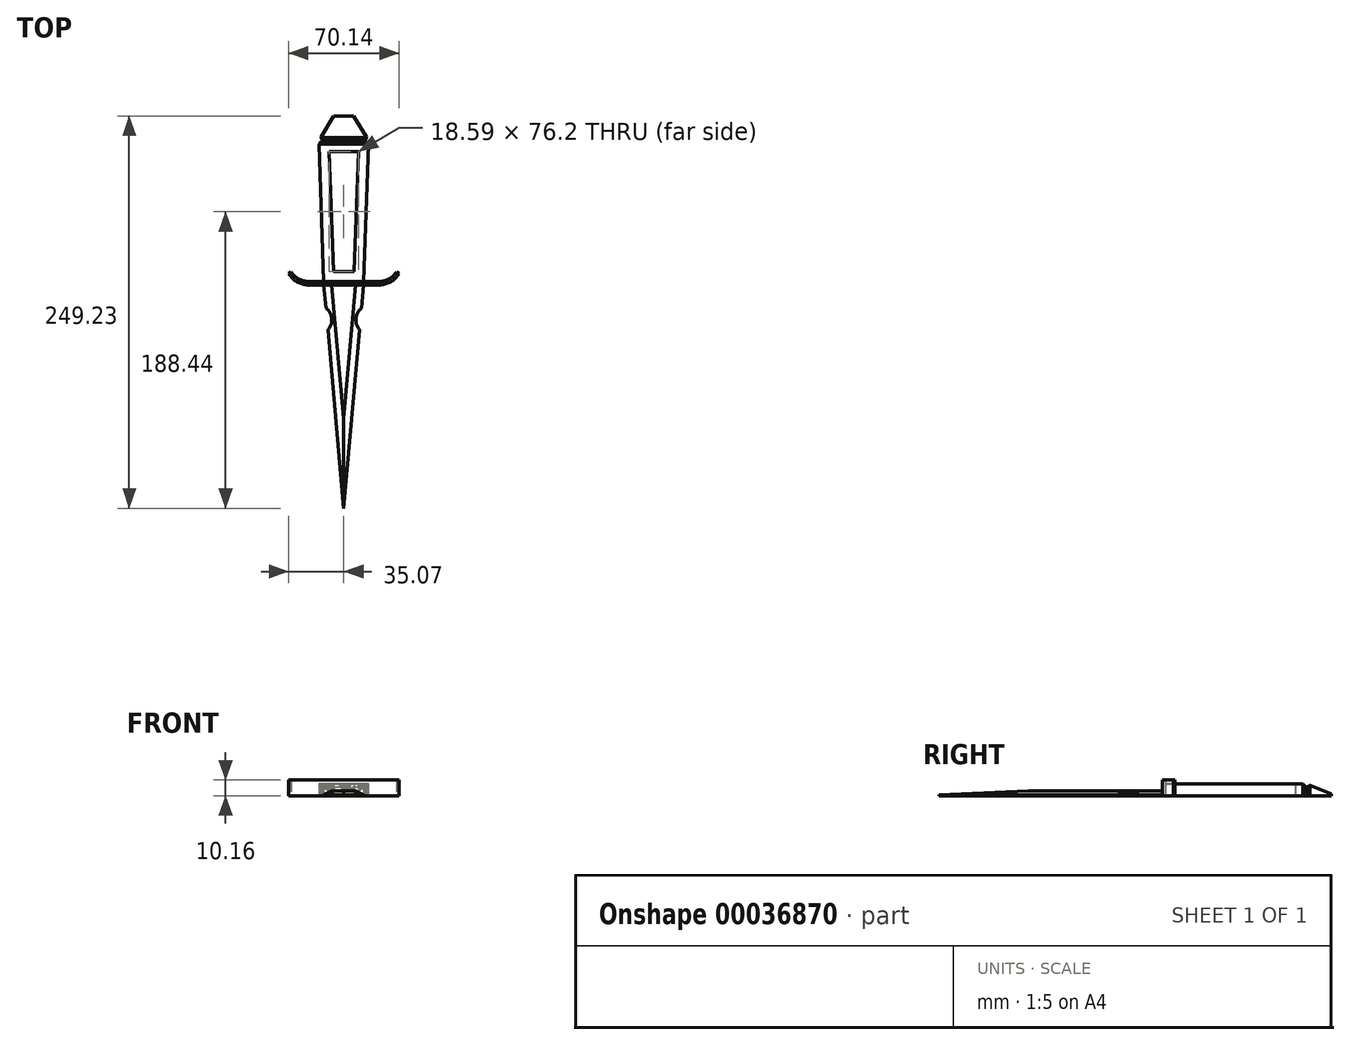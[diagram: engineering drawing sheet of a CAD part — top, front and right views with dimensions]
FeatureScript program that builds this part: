
annotation { "Feature Type Name" : "Feature", "Feature Type Description" : "" }
export const myFeature = defineFeature(function(context is Context, id is Id, definition is map)
    precondition{}
    {
        {
            var Q0;
            Q0=qCreatedBy(makeId("Top.planeOp"),FACE);
            var sketch = newSketch(context, id + "F0", { "sketchPlane" : qUnion([Q0])});
            skLineSegment(sketch, "E0", {"start": v(-12.7, 0) * mm, "end": v(-15.88, 88.9) * mm});
            skLineSegment(sketch, "E1", {"start": v(-15.88, 88.9) * mm, "end": v(15.87, 88.9) * mm});
            skLineSegment(sketch, "E2", {"start": v(15.87, 88.9) * mm, "end": v(12.7, 0) * mm});
            skLineSegment(sketch, "E3", {"start": v(12.7, 0) * mm, "end": v(-12.7, 0) * mm});
            skLineSegment(sketch, "E4", {"start": v(0, 0) * mm, "end": v(0, -100.11) * mm, "construction": true});
            skLineSegment(sketch, "E5.0", {"start": v(-9.3, 82.55) * mm, "end": v(9.3, 82.55) * mm});
            skLineSegment(sketch, "E5.1", {"start": v(-6.57, 6.35) * mm, "end": v(-9.3, 82.55) * mm});
            skLineSegment(sketch, "E5.2", {"start": v(6.57, 6.35) * mm, "end": v(-6.57, 6.35) * mm});
            skLineSegment(sketch, "E5.3", {"start": v(9.3, 82.55) * mm, "end": v(6.57, 6.35) * mm});
            skSolve(sketch);
        }
        {
            var Q0;
            Q0 = qSketchRegion(id + "F0", true);
            extrude(context, id + "F1", {"entities" : qUnion([Q0]), "depth" : 7.62 * mm});
        }
        {
            var Q0;
            Q0=makeQuery(id+"F1.opExtrude","SWEPT_FACE",FACE,{"disambiguationData":[OSD([sQuery(id+"F0.wireOp",EDGE,"E1")])]});
            var sketch = newSketch(context, id + "F2", { "sketchPlane" : qUnion([Q0])});
            skLineSegment(sketch, "E6.0", {"start": v(13.34, 5.08) * mm, "end": v(13.34, 0) * mm});
            skLineSegment(sketch, "E6.1", {"start": v(13.34, 5.08) * mm, "end": v(-13.33, 5.08) * mm});
            skLineSegment(sketch, "E6.2", {"start": v(-13.33, 5.08) * mm, "end": v(-13.33, 0) * mm});
            skLineSegment(sketch, "E7", {"start": v(13.34, 0) * mm, "end": v(-13.33, 0) * mm});
            skSolve(sketch);
        }
        {
            var Q0;
            Q0 = qSketchRegion(id + "F2", true);
            extrude(context, id + "F3", {"entities" : qUnion([Q0]), "operationType" : NewBodyOperationType.ADD, "depth" : 0.5 * mm});
        }
        {
            var Q0;
            Q0=qCreatedBy(makeId("Top.planeOp"),FACE);
            var sketch = newSketch(context, id + "F4", { "sketchPlane" : qUnion([Q0])});
            skLineSegment(sketch, "E8", {"start": v(-15.88, 89.4) * mm, "end": v(15.87, 89.4) * mm});
            skLineSegment(sketch, "E9", {"start": v(15.87, 89.4) * mm, "end": v(6.35, 105.24) * mm});
            skLineSegment(sketch, "E10", {"start": v(6.35, 105.24) * mm, "end": v(-6.35, 105.24) * mm});
            skLineSegment(sketch, "E11", {"start": v(-6.35, 105.24) * mm, "end": v(-15.88, 89.4) * mm});
            skSolve(sketch);
        }
        {
            var Q0;
            Q0 = qSketchRegion(id + "F4", true);
            var Q1;
            Q1=makeQuery(id+"F1.opExtrude","CAP_FACE",FACE,{"disambiguationData":[OSD([sQuery(id+"F0.wireOp",EDGE,"E0"),sQuery(id+"F0.wireOp",EDGE,"E1"),sQuery(id+"F0.wireOp",EDGE,"E2"),sQuery(id+"F0.wireOp",EDGE,"E3"),sQuery(id+"F0.wireOp",EDGE,"E5.0"),sQuery(id+"F0.wireOp",EDGE,"E5.1"),sQuery(id+"F0.wireOp",EDGE,"E5.2"),sQuery(id+"F0.wireOp",EDGE,"E5.3")])],"isStart":false});
            extrude(context, id + "F5", {"entities" : qUnion([Q0]), "operationType" : NewBodyOperationType.ADD, "endBound" : BoundingType.UP_TO_SURFACE, "endBoundEntityFace" : qUnion([Q1]), "depth" : 25.4 * mm});
        }
        {
            var Q0;
            Q0=qCreatedBy(makeId("Right.planeOp"),FACE);
            var sketch = newSketch(context, id + "F6", { "sketchPlane" : qUnion([Q0])});
            skLineSegment(sketch, "E12", {"start": v(89.4, 7.62) * mm, "end": v(105.24, 1.27) * mm});
            skLineSegment(sketch, "E13", {"start": v(105.24, 1.27) * mm, "end": v(105.24, 7.62) * mm});
            skLineSegment(sketch, "E14", {"start": v(105.24, 7.62) * mm, "end": v(89.4, 7.62) * mm});
            skSolve(sketch);
        }
        {
            var Q0;
            Q0 = qSketchRegion(id + "F6", true);
            extrude(context, id + "F7", {"entities" : qUnion([Q0]), "operationType" : NewBodyOperationType.REMOVE, "endBound" : BoundingType.SYMMETRIC, "oppositeDirection" : true, "depth" : 50.8 * mm});
        }
        {
            var Q0;
            Q0=makeQuery(id+"F1.opExtrude","CAP_EDGE",EDGE,{"disambiguationData":[OSD([sQuery(id+"F0.wireOp",EDGE,"E1")])],"isStart":false});
            var Q1;
            Q1=makeQuery(id+"F7.boolean.opBoolean","MERGE",EDGE,{"derivedFrom":[makeQuery(id+"F5.opExtrude","CAP_EDGE",EDGE,{"disambiguationData":[OSD([sQuery(id+"F4.wireOp",EDGE,"E8")])],"isStart":false})],"fromTools":[makeQuery(id+"F7.opExtrude","SWEPT_EDGE",EDGE,{"disambiguationData":[OSD([sQuery(id+"F6.wireOp",EDGE,"E12"),sQuery(id+"F6.wireOp",EDGE,"E14")])]})]});
            var Q2;
            Q2=makeQuery(id+"F1.opExtrude","SWEPT_EDGE",EDGE,{"disambiguationData":[OSD([sQuery(id+"F0.wireOp",EDGE,"E1"),sQuery(id+"F0.wireOp",EDGE,"E2")])]});
            var Q3;
            Q3=makeQuery(id+"F5.opExtrude","SWEPT_EDGE",EDGE,{"disambiguationData":[OSD([sQuery(id+"F4.wireOp",EDGE,"E8"),sQuery(id+"F4.wireOp",EDGE,"E9")])]});
            var Q4;
            Q4=makeQuery(id+"F5.opExtrude","SWEPT_EDGE",EDGE,{"disambiguationData":[OSD([sQuery(id+"F4.wireOp",EDGE,"E8"),sQuery(id+"F4.wireOp",EDGE,"E11")])]});
            var Q5;
            Q5=makeQuery(id+"F1.opExtrude","SWEPT_EDGE",EDGE,{"disambiguationData":[OSD([sQuery(id+"F0.wireOp",EDGE,"E0"),sQuery(id+"F0.wireOp",EDGE,"E1")])]});
            chamfer(context, id + "F8", {"entities" : qUnion([Q0, Q1, Q2, Q3, Q4, Q5]), "width" : 1.52 * mm, "tangentPropagation" : true});
        }
        {
            var Q0;
            Q0=qCreatedBy(makeId("Top.planeOp"),FACE);
            var sketch = newSketch(context, id + "F9", { "sketchPlane" : qUnion([Q0])});
            skLineSegment(sketch, "E15", {"start": v(-22.23, 0) * mm, "end": v(22.23, 0) * mm});
            skArc(sketch, "E16", {"start": v(-33.36, 6.1) * mm, "mid": v(-28.58, 1.63) * mm, "end": v(-22.23, 0) * mm});
            skArc(sketch, "E17", {"start": v(22.23, 0) * mm, "mid": v(28.58, 1.63) * mm, "end": v(33.36, 6.1) * mm});
            skArc(sketch, "E18.0", {"start": v(22.23, -2.03) * mm, "mid": v(29.55, -0.16) * mm, "end": v(35.07, 5.01) * mm});
            skLineSegment(sketch, "E18.1", {"start": v(-22.23, -2.03) * mm, "end": v(22.23, -2.03) * mm});
            skArc(sketch, "E18.2", {"start": v(-35.07, 5.01) * mm, "mid": v(-29.55, -0.16) * mm, "end": v(-22.23, -2.03) * mm});
            skLineSegment(sketch, "E19", {"start": v(-35.07, 5.01) * mm, "end": v(-33.36, 6.1) * mm});
            skLineSegment(sketch, "E20", {"start": v(33.36, 6.1) * mm, "end": v(35.07, 5.01) * mm});
            skSolve(sketch);
        }
        {
            var Q0;
            Q0 = qSketchRegion(id + "F9", true);
            extrude(context, id + "F10", {"entities" : qUnion([Q0]), "operationType" : NewBodyOperationType.ADD, "depth" : 10.16 * mm});
        }
        {
            var Q0;
            Q0=qCreatedBy(makeId("Top.planeOp"),FACE);
            var sketch = newSketch(context, id + "F11", { "sketchPlane" : qUnion([Q0])});
            skLineSegment(sketch, "E21", {"start": v(0, 112.3) * mm, "end": v(-127.44, -2.4) * mm, "construction": true});
            skLineSegment(sketch, "E22", {"start": v(-127.44, -2.4) * mm, "end": v(0, -144) * mm, "construction": true});
            skLineSegment(sketch, "E23", {"start": v(0, -144) * mm, "end": v(127.44, -29.3) * mm, "construction": true});
            skLineSegment(sketch, "E24", {"start": v(127.44, -29.3) * mm, "end": v(0, 112.3) * mm, "construction": true});
            skLineSegment(sketch, "E25", {"start": v(-12.7, -2.03) * mm, "end": v(-11.4, -16.67) * mm});
            skLineSegment(sketch, "E26", {"start": v(12.7, -2.03) * mm, "end": v(11.4, -16.67) * mm});
            skLineSegment(sketch, "E27", {"start": v(-12.7, -2.03) * mm, "end": v(12.7, -2.03) * mm});
            skArc(sketch, "E28", {"start": v(-10.13, -30.7) * mm, "mid": v(-7.66, -23.4) * mm, "end": v(-11.4, -16.67) * mm});
            skArc(sketch, "E29", {"start": v(11.4, -16.67) * mm, "mid": v(7.66, -23.4) * mm, "end": v(10.13, -30.7) * mm});
            skLineSegment(sketch, "E30", {"start": v(0, 112.3) * mm, "end": v(0, -144) * mm, "construction": true});
            skLineSegment(sketch, "E31.trimOffspring", {"start": v(-10.13, -30.7) * mm, "end": v(0, -144) * mm});
            skLineSegment(sketch, "E32.trimOffspring", {"start": v(10.13, -30.7) * mm, "end": v(0, -144) * mm});
            skSolve(sketch);
        }
        {
            var Q0;
            Q0 = qSketchRegion(id + "F11", true);
            extrude(context, id + "F12", {"entities" : qUnion([Q0]), "operationType" : NewBodyOperationType.ADD, "depth" : 3.17 * mm});
        }
        {
            var Q0;
            Q0=makeQuery(id+"F12.opExtrude","CAP_EDGE",EDGE,{"disambiguationData":[OSD([sQuery(id+"F11.wireOp",EDGE,"E32.trimOffspring")])],"isStart":false});
            var Q1;
            Q1=makeQuery(id+"F12.opExtrude","CAP_EDGE",EDGE,{"disambiguationData":[OSD([sQuery(id+"F11.wireOp",EDGE,"E31.trimOffspring")])],"isStart":false});
            chamfer(context, id + "F13", {"entities" : qUnion([Q0, Q1]), "chamferType" : ChamferType.TWO_OFFSETS, "width1" : 2.54 * mm, "oppositeDirection" : false, "width2" : 5.08 * mm, "tangentPropagation" : true});
        }
    });
